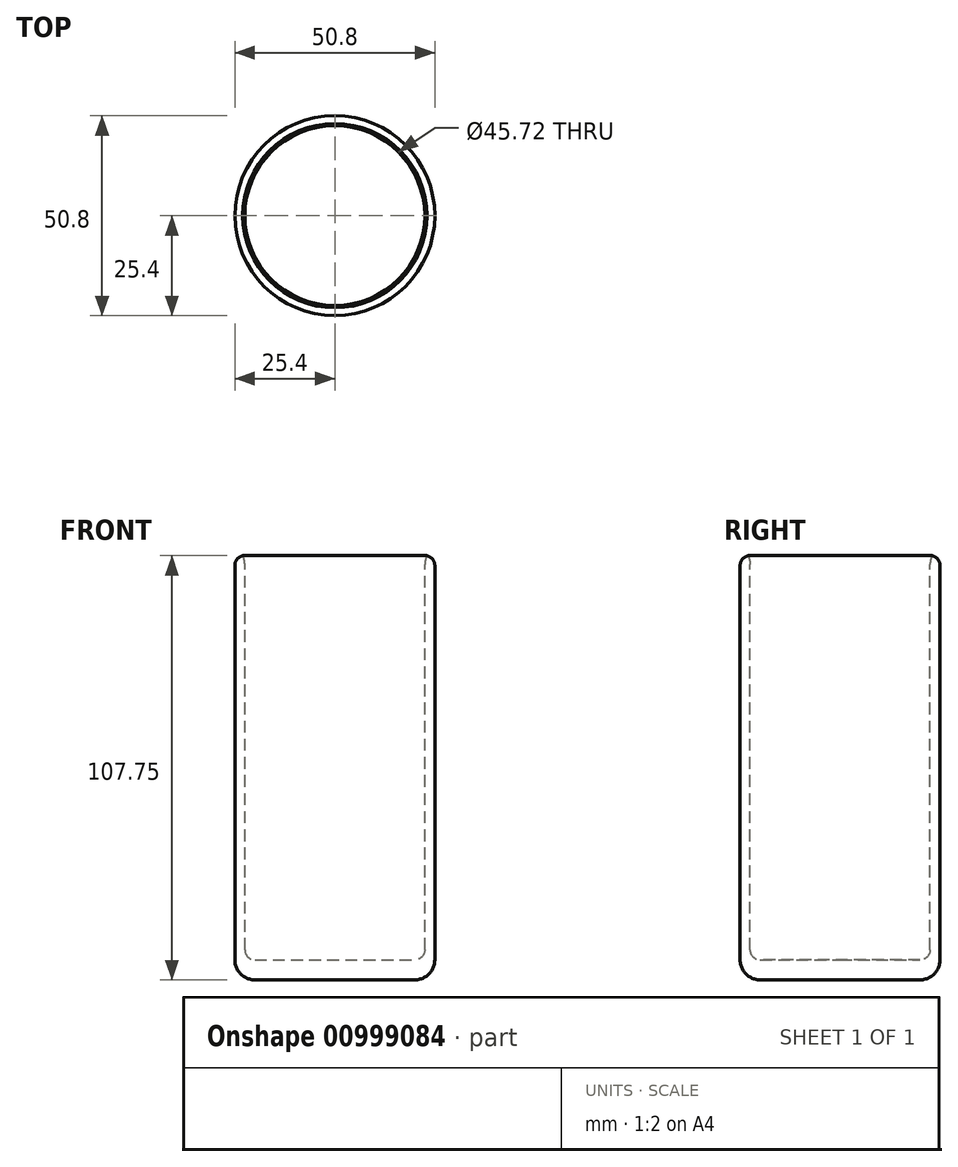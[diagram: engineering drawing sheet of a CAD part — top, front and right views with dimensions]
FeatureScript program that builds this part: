
annotation { "Feature Type Name" : "Feature", "Feature Type Description" : "" }
export const myFeature = defineFeature(function(context is Context, id is Id, definition is map)
    precondition{}
    {
        {
            var Q0;
            Q0=qCreatedBy(makeId("Front.planeOp"),FACE);
            var sketch = newSketch(context, id + "F0", { "sketchPlane" : qUnion([Q0])});
            skLineSegment(sketch, "E0", {"start": v(-25.4, 14.98) * mm, "end": v(-22.86, 9.9) * mm});
            skLineSegment(sketch, "E1", {"start": v(-22.86, 9.9) * mm, "end": v(-22.86, -91.7) * mm});
            skLineSegment(sketch, "E2", {"start": v(-22.86, -91.7) * mm, "end": v(0, -91.7) * mm});
            skLineSegment(sketch, "E3", {"start": v(0, -91.7) * mm, "end": v(0, -96.78) * mm});
            skLineSegment(sketch, "E4", {"start": v(0, -96.78) * mm, "end": v(-25.4, -96.78) * mm});
            skLineSegment(sketch, "E5", {"start": v(-25.4, -96.78) * mm, "end": v(-25.4, 14.98) * mm});
            skSolve(sketch);
        }
        {
            var Q0;
            Q0=makeQuery(id+"F0.imprint","IMPRINT",FACE,{"disambiguationData":[TD([[makeQuery(id+"F0.imprint","IMPRINT",EDGE,{"derivedFrom":sQuery(id+"F0.wireOp",EDGE,"E0")}),-1.0]])]});
            var Q1;
            Q1=sQuery(id+"F0.wireOp",EDGE,"E3");
            revolve(context, id + "F1", {"surfaceOperationType" : NewSurfaceOperationType.NEW, "entities" : qUnion([Q0]), "axis" : qUnion([Q1]), "revolveType" : RevolveType.FULL});
        }
        {
            var Q0;
            Q0=makeQuery(id+"F1.opRevolve","SWEPT_EDGE",EDGE,{"disambiguationData":[OSD([sQuery(id+"F0.wireOp",EDGE,"E4"),sQuery(id+"F0.wireOp",EDGE,"E5")])]});
            fillet(context, id + "F2", {"entities" : qUnion([Q0]), "radius" : 5.08 * mm, "tangentPropagation" : true, "allowEdgeOverflow" : false});
        }
        {
            var Q0;
            Q0=makeQuery(id+"F1.opRevolve","SWEPT_EDGE",EDGE,{"disambiguationData":[OSD([sQuery(id+"F0.wireOp",EDGE,"E0"),sQuery(id+"F0.wireOp",EDGE,"E1")])]});
            fillet(context, id + "F3", {"entities" : qUnion([Q0]), "radius" : 5.08 * mm, "tangentPropagation" : true, "allowEdgeOverflow" : false});
        }
        {
            var Q0;
            Q0=makeQuery(id+"F1.opRevolve","SWEPT_EDGE",EDGE,{"disambiguationData":[OSD([sQuery(id+"F0.wireOp",EDGE,"E0"),sQuery(id+"F0.wireOp",EDGE,"E5")])]});
            var Q1;
            Q1=makeQuery(id+"F1.opRevolve","SWEPT_EDGE",EDGE,{"disambiguationData":[OSD([sQuery(id+"F0.wireOp",EDGE,"E1"),sQuery(id+"F0.wireOp",EDGE,"E2")])]});
            fillet(context, id + "F4", {"entities" : qUnion([Q0, Q1]), "radius" : 2.54 * mm, "tangentPropagation" : true, "allowEdgeOverflow" : false});
        }
    });
